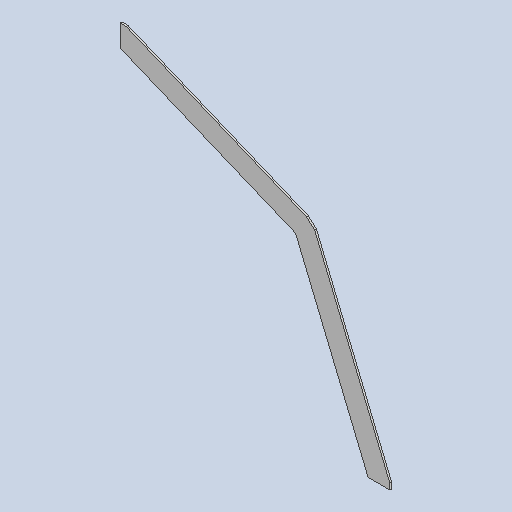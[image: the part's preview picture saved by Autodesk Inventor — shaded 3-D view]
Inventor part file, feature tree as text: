
AUTODESK INVENTOR PART (.ipt)
format: ipt  version: 2025 (Build 290162010, 162A)  size: 135,168 bytes
history: native  units: mm
features: other x5, sheet_metal_op x1, sketch x1
ambient origin geometry x8: Origin, YZ Plane, XZ Plane, XY Plane, X Axis, Y Axis, Z Axis, Center Point
bodies: Solid1 (feature_tree)
feature tree (7):
  sheet_metal_op  "Face1"
  other  "Corner Chamfer1"
  other  "Corner Chamfer2"
  other  "Corner Chamfer3"
  sketch  "Sketch1"  dims[d6=513.0mm d15=2.0mm d16=25.0mm d17=7.0mm d18=6.0mm d19=22.5deg d20=7.0mm d21=6.0mm d22=22.5deg d23=6.0mm d24=6.0mm d25=4.363323mm]
  other  "Plate1"
  other  "Definition1"
